# Revit family: НЕВАТОМ_Нaгреватель NEP-E, Версия 2
name_source: partatom
category: Оборудование
revit_build: Autodesk Revit 2017 (Build: 20170118_1100(x64)
units: mm (PartAtom-declared; Revit-internal decimal feet)

## family parameters
Всегда вертикально = Да
На основе рабочей плоскости = Нет
Общий = Нет
При загрузке вырезать с полостями = Нет
Размер круглого соединителя = Использовать диаметр
Тип детали = Нормальный
Точка расчета площади = Нет

## types (1)
- Нагреватель электрический NEP-E
    A = 500 мм
    A+42 = 542 мм
    ADSK_Единица измерения = шт.
    ADSK_Завод-изготовитель = НЕВАТОМ
    ADSK_Количество = 1
    ADSK_Количество фаз числовое = 3
    ADSK_Коэффициент мощности = 0.548246
    ADSK_Марка = NEP-E-500-300/7.5
    ADSK_Масса = 12
    ADSK_Наименование = Нагреватель электрический прямоугольный с комплектом автоматики
    ADSK_Напряжение = 380 В
    ADSK_Номинальная мощность = 8 кВт
    ADSK_Полная мощность = 13680 В·А
    ADSK_Примечание = Подбор через ADSK_Номинальная мощность и НЕВАТОМ_Минимальный расход воздуха
    ADSK_Температура воздуха на входе в нагреватель = -37 °C
    ADSK_Температура воздуха на выходе из нагревателя = -10 °C
    ADSK_Ток = 12 А
    B = 300 мм
    B2 = 148 мм
    B3 = 225 мм
    C = 342 мм
    H = 690 мм
    K = 9 мм
    L = 536 мм
    L2 = 375 мм
    Материал = Сталь оцинкованная
    НЕВАТОМ_NEIVA = нет данных
    НЕВАТОМ_URL = https://t.me
    НЕВАТОМ_Минимальный расход воздуха = 810.0 м³/ч
